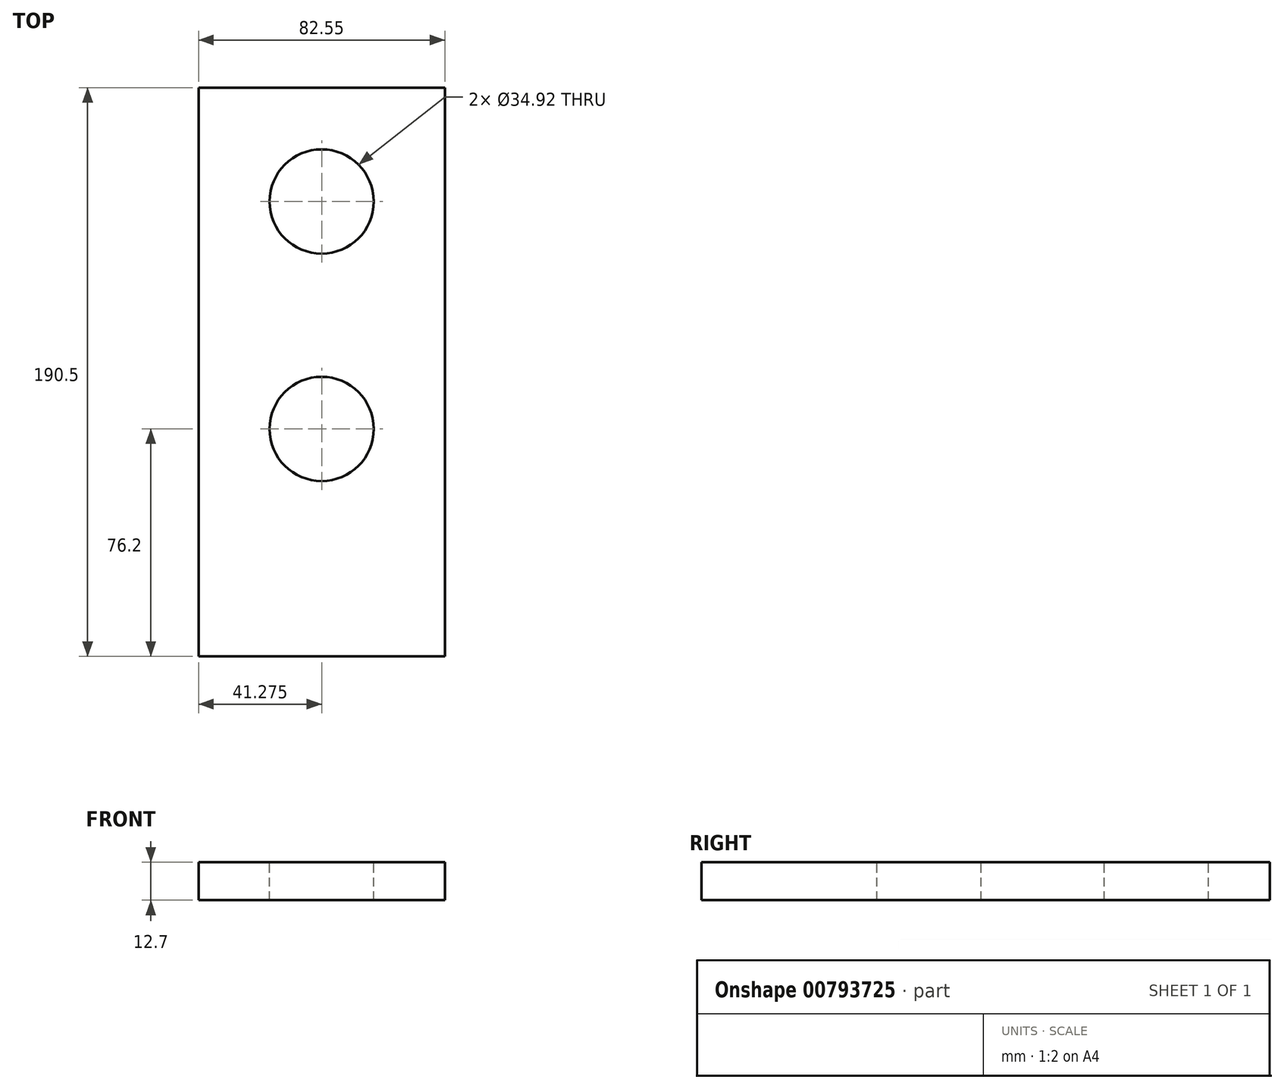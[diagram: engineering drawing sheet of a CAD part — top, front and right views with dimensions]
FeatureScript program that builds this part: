
annotation { "Feature Type Name" : "Feature", "Feature Type Description" : "" }
export const myFeature = defineFeature(function(context is Context, id is Id, definition is map)
    precondition{}
    {
        {
            var Q0;
            Q0=qCreatedBy(makeId("Right.planeOp"),FACE);
            var sketch = newSketch(context, id + "F0", { "sketchPlane" : qUnion([Q0])});
            skLineSegment(sketch, "E0", {"start": v(0, 0) * mm, "end": v(190.5, 0) * mm});
            skLineSegment(sketch, "E1", {"start": v(190.5, 0) * mm, "end": v(190.5, 12.7) * mm});
            skLineSegment(sketch, "E2", {"start": v(190.5, 12.7) * mm, "end": v(25.4, 12.7) * mm});
            skLineSegment(sketch, "E3", {"start": v(0, 0) * mm, "end": v(0, 127) * mm});
            skLineSegment(sketch, "E4", {"start": v(0, 127) * mm, "end": v(25.4, 127) * mm});
            skLineSegment(sketch, "E5", {"start": v(25.4, 127) * mm, "end": v(25.4, 12.7) * mm});
            skSolve(sketch);
        }
        {
            var Q0;
            Q0 = qSketchRegion(id + "F0", true);
            extrude(context, id + "F1", {"entities" : qUnion([Q0]), "depth" : 82.55 * mm, "offsetDistance" : 25.4 * mm});
        }
        {
            var Q0;
            Q0=makeQuery(id+"F1.opExtrude","SWEPT_FACE",FACE,{"disambiguationData":[OSD([sQuery(id+"F0.wireOp",EDGE,"E2")])]});
            var sketch = newSketch(context, id + "F2", { "sketchPlane" : qUnion([Q0])});
            skLineSegment(sketch, "E6", {"start": v(41.28, 190.5) * mm, "end": v(41.28, 152.4) * mm, "construction": true});
            skLineSegment(sketch, "E7", {"start": v(41.28, 152.4) * mm, "end": v(41.28, 76.2) * mm, "construction": true});
            skCircle(sketch, "E8", {"center": v(41.28, 76.2) * mm, "radius": 17.46 * mm});
            skCircle(sketch, "E9", {"center": v(41.28, 152.4) * mm, "radius": 17.46 * mm});
            skSolve(sketch);
        }
        {
            var Q0;
            Q0 = qSketchRegion(id + "F2", true);
            extrude(context, id + "F3", {"entities" : qUnion([Q0]), "operationType" : NewBodyOperationType.REMOVE, "oppositeDirection" : true, "depth" : 25.4 * mm, "offsetDistance" : 25.4 * mm});
        }
        {
            var Q0;
            Q0=makeQuery(id+"F1.opExtrude","SWEPT_FACE",FACE,{"disambiguationData":[OSD([sQuery(id+"F0.wireOp",EDGE,"E5")])]});
            var sketch = newSketch(context, id + "F4", { "sketchPlane" : qUnion([Q0])});
            skLineSegment(sketch, "E10", {"start": v(-41.28, 127) * mm, "end": v(-41.28, 78.31) * mm, "construction": true});
            skSolve(sketch);
        }
        {
            var Q0;
            {var subQ0=sQuery(id+"F0.wireOp",EDGE,"E5");Q0=makeQuery(id+"F4.imprint","IMPRINT",FACE,{"disambiguationData":[TD([[makeQuery(id+"F4.imprint","IMPRINT",EDGE,{"derivedFrom":makeQuery(id+"F1.opExtrude","CAP_EDGE",EDGE,{"disambiguationData":[OSD([subQ0])],"isStart":true})}),-1.0]])]});}
            extrude(context, id + "F5", {"entities" : qUnion([Q0]), "operationType" : NewBodyOperationType.REMOVE, "endBound" : BoundingType.THROUGH_ALL, "oppositeDirection" : true, "depth" : 25.4 * mm, "offsetDistance" : 25.4 * mm});
        }
    });
